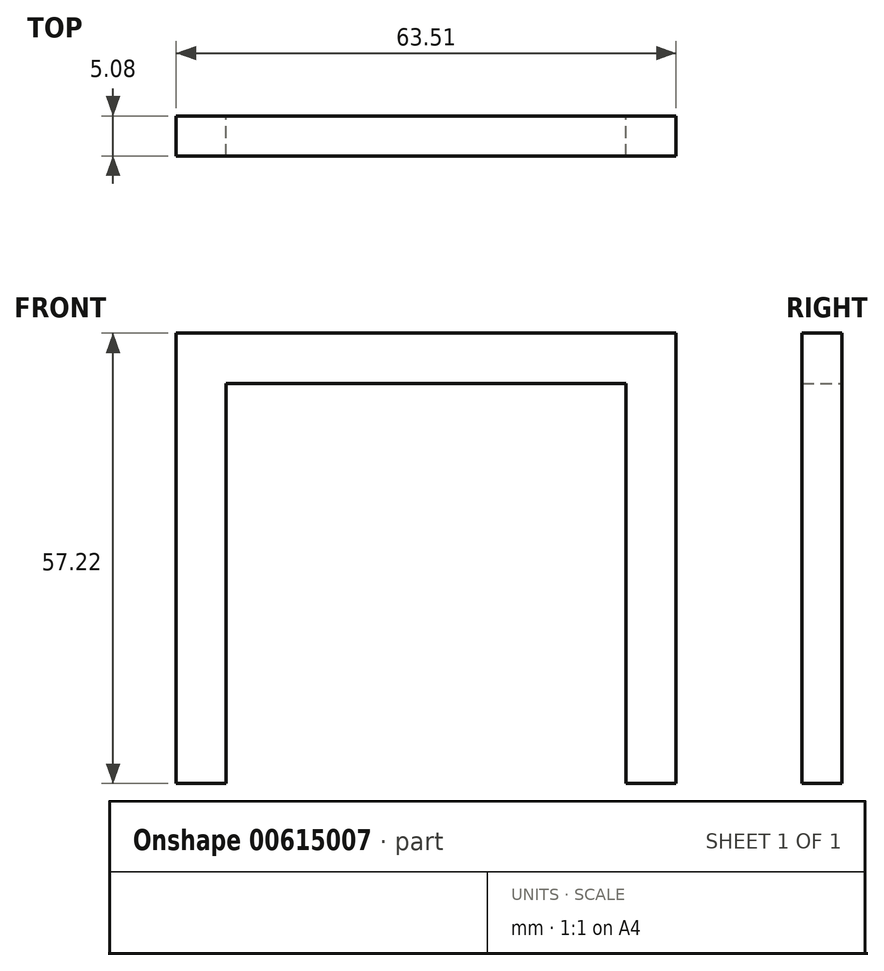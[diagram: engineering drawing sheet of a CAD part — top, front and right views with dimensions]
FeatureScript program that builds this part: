
annotation { "Feature Type Name" : "Feature", "Feature Type Description" : "" }
export const myFeature = defineFeature(function(context is Context, id is Id, definition is map)
    precondition{}
    {
        {
            var Q0;
            Q0=qCreatedBy(makeId("Front.planeOp"),FACE);
            var sketch = newSketch(context, id + "F0", { "sketchPlane" : qUnion([Q0])});
            skLineSegment(sketch, "E0", {"start": v(-26.19, 22.82) * mm, "end": v(-26.19, -27.98) * mm});
            skLineSegment(sketch, "E1", {"start": v(-26.19, 22.82) * mm, "end": v(24.61, 22.82) * mm});
            skLineSegment(sketch, "E2", {"start": v(24.61, 22.82) * mm, "end": v(24.61, -27.98) * mm});
            skLineSegment(sketch, "E3", {"start": v(-26.19, -27.98) * mm, "end": v(-32.54, -27.98) * mm});
            skLineSegment(sketch, "E4", {"start": v(-32.54, -27.98) * mm, "end": v(-32.54, 22.95) * mm});
            skLineSegment(sketch, "E5", {"start": v(-32.54, 22.95) * mm, "end": v(-32.54, 29.24) * mm});
            skLineSegment(sketch, "E6", {"start": v(-32.54, 29.24) * mm, "end": v(24.68, 29.24) * mm});
            skLineSegment(sketch, "E7", {"start": v(24.68, 29.24) * mm, "end": v(30.97, 29.24) * mm});
            skLineSegment(sketch, "E8", {"start": v(30.97, 29.24) * mm, "end": v(30.97, -27.98) * mm});
            skLineSegment(sketch, "E9", {"start": v(30.97, -27.98) * mm, "end": v(24.61, -27.98) * mm});
            skSolve(sketch);
        }
        {
            var Q0;
            Q0 = qSketchRegion(id + "F0", true);
            extrude(context, id + "F1", {"entities" : qUnion([Q0]), "depth" : 5.08 * mm, "offsetDistance" : 25.4 * mm});
        }
    });
